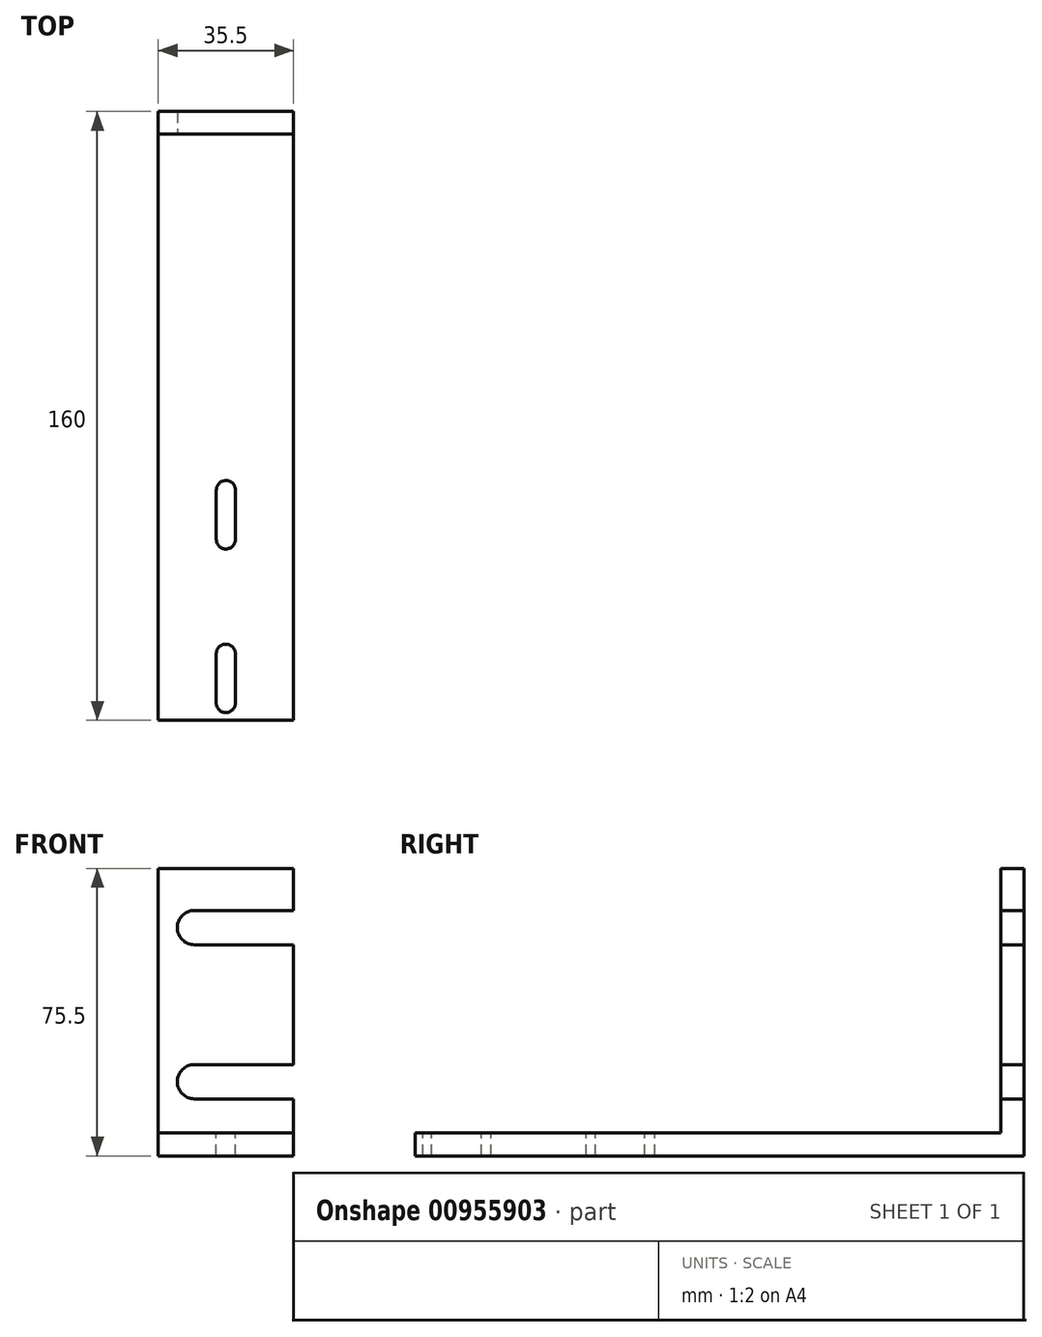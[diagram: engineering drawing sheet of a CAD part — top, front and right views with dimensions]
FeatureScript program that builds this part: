
annotation { "Feature Type Name" : "Feature", "Feature Type Description" : "" }
export const myFeature = defineFeature(function(context is Context, id is Id, definition is map)
    precondition{}
    {
        {
            var Q0;
            Q0=qCreatedBy(makeId("Front.planeOp"),FACE);
            var sketch = newSketch(context, id + "F0", { "sketchPlane" : qUnion([Q0])});
            skLineSegment(sketch, "E0.bottom", {"start": v(17.75, 3) * mm, "end": v(-17.75, 3) * mm});
            skLineSegment(sketch, "E0.top", {"start": v(17.75, -3) * mm, "end": v(-17.75, -3) * mm});
            skLineSegment(sketch, "E0.left", {"start": v(17.75, 3) * mm, "end": v(17.75, -3) * mm});
            skLineSegment(sketch, "E0.right", {"start": v(-17.75, 3) * mm, "end": v(-17.75, -3) * mm});
            skPoint(sketch, "E0.middle", {"position": v(0, 0) * mm});
            skSolve(sketch);
        }
        {
            var Q0;
            Q0=makeQuery(id+"F0.imprint","IMPRINT",FACE,{"disambiguationData":[TD([[makeQuery(id+"F0.imprint","IMPRINT",EDGE,{"derivedFrom":sQuery(id+"F0.wireOp",EDGE,"E0.bottom")}),1.0]])]});
            extrude(context, id + "F1", {"entities" : qUnion([Q0]), "depth" : 160 * mm, "offsetDistance" : 25 * mm});
        }
        {
            var Q0;
            Q0=makeQuery(id+"F1.opExtrude","SWEPT_FACE",FACE,{"disambiguationData":[OSD([sQuery(id+"F0.wireOp",EDGE,"E0.bottom")])]});
            var sketch = newSketch(context, id + "F2", { "sketchPlane" : qUnion([Q0])});
            skLineSegment(sketch, "E1.bottom", {"start": v(17.75, -6) * mm, "end": v(-17.75, -6) * mm});
            skLineSegment(sketch, "E1.top", {"start": v(17.75, 0) * mm, "end": v(-17.75, 0) * mm});
            skLineSegment(sketch, "E1.left", {"start": v(17.75, -6) * mm, "end": v(17.75, 0) * mm});
            skLineSegment(sketch, "E1.right", {"start": v(-17.75, -6) * mm, "end": v(-17.75, 0) * mm});
            skSolve(sketch);
        }
        {
            var Q0;
            Q0=makeQuery(id+"F2.imprint","IMPRINT",FACE,{"disambiguationData":[TD([[makeQuery(id+"F2.imprint","IMPRINT",EDGE,{"derivedFrom":sQuery(id+"F2.wireOp",EDGE,"E1.bottom")}),-1.0]])]});
            extrude(context, id + "F3", {"entities" : qUnion([Q0]), "operationType" : NewBodyOperationType.ADD, "depth" : 69.5 * mm, "offsetDistance" : 25 * mm});
        }
        {
            var Q0;
            Q0=makeQuery(id+"F1.opExtrude","SWEPT_FACE",FACE,{"disambiguationData":[OSD([sQuery(id+"F0.wireOp",EDGE,"E0.bottom")])]});
            var sketch = newSketch(context, id + "F4", { "sketchPlane" : qUnion([Q0])});
            skArc(sketch, "E2", {"start": v(2.5, -142.63) * mm, "mid": v(0.07, -140) * mm, "end": v(-2.5, -142.5) * mm});
            skArc(sketch, "E3", {"start": v(-2.5, -155.5) * mm, "mid": v(0.07, -158) * mm, "end": v(2.5, -155.37) * mm});
            skLineSegment(sketch, "E4", {"start": v(-2.5, -142.5) * mm, "end": v(-2.5, -155.5) * mm});
            skLineSegment(sketch, "E5", {"start": v(2.5, -142.63) * mm, "end": v(2.5, -155.63) * mm});
            skArc(sketch, "E6", {"start": v(2.5, -99.63) * mm, "mid": v(0.07, -97) * mm, "end": v(-2.5, -99.5) * mm});
            skArc(sketch, "E7", {"start": v(-2.5, -112.5) * mm, "mid": v(0.07, -115) * mm, "end": v(2.5, -112.37) * mm});
            skLineSegment(sketch, "E8", {"start": v(-2.5, -99.5) * mm, "end": v(-2.5, -112.5) * mm});
            skLineSegment(sketch, "E9", {"start": v(2.5, -99.63) * mm, "end": v(2.5, -112.63) * mm});
            skPoint(sketch, "E10", {"position": v(0, -101.51) * mm});
            skSolve(sketch);
        }
        {
            var Q0;
            {var subQ1=sQuery(id+"F4.wireOp",EDGE,"E6");Q0=makeQuery(id+"F4.imprint","IMPRINT",FACE,{"disambiguationData":[TD([[makeQuery(id+"F4.imprint","IMPRINT",EDGE,{"derivedFrom":subQ1}),1.0]])]});}
            extrude(context, id + "F5", {"entities" : qUnion([Q0]), "operationType" : NewBodyOperationType.REMOVE, "oppositeDirection" : true, "depth" : 25 * mm, "offsetDistance" : 25 * mm});
        }
        {
            var Q0;
            {var subQ1=sQuery(id+"F4.wireOp",EDGE,"E2");Q0=makeQuery(id+"F4.imprint","IMPRINT",FACE,{"disambiguationData":[TD([[makeQuery(id+"F4.imprint","IMPRINT",EDGE,{"derivedFrom":subQ1}),1.0]])]});}
            extrude(context, id + "F6", {"entities" : qUnion([Q0]), "operationType" : NewBodyOperationType.REMOVE, "oppositeDirection" : true, "depth" : 25 * mm, "offsetDistance" : 25 * mm});
        }
        {
            var Q0;
            Q0=makeQuery(id+"F3.opExtrude","SWEPT_FACE",FACE,{"disambiguationData":[OSD([sQuery(id+"F2.wireOp",EDGE,"E1.bottom")])]});
            var sketch = newSketch(context, id + "F7", { "sketchPlane" : qUnion([Q0])});
            skArc(sketch, "E11", {"start": v(-8.25, 21) * mm, "mid": v(-12.75, 16.5) * mm, "end": v(-8.25, 12) * mm});
            skLineSegment(sketch, "E12", {"start": v(-8.25, 21) * mm, "end": v(17.75, 21) * mm});
            skLineSegment(sketch, "E13", {"start": v(-8.25, 12) * mm, "end": v(17.75, 12) * mm});
            skArc(sketch, "E14", {"start": v(-8.25, 61.5) * mm, "mid": v(-12.75, 57) * mm, "end": v(-8.25, 52.5) * mm});
            skLineSegment(sketch, "E15", {"start": v(-8.25, 61.5) * mm, "end": v(17.75, 61.5) * mm});
            skLineSegment(sketch, "E16", {"start": v(-8.25, 52.5) * mm, "end": v(17.75, 52.5) * mm});
            skSolve(sketch);
        }
        {
            var Q0;
            Q0=makeQuery(id+"F7.imprint","IMPRINT",FACE,{"disambiguationData":[TD([[makeQuery(id+"F7.imprint","IMPRINT",EDGE,{"derivedFrom":sQuery(id+"F7.wireOp",EDGE,"E14")}),1.0]])]});
            var Q1;
            Q1=makeQuery(id+"F7.imprint","IMPRINT",FACE,{"disambiguationData":[TD([[makeQuery(id+"F7.imprint","IMPRINT",EDGE,{"derivedFrom":sQuery(id+"F7.wireOp",EDGE,"E11")}),1.0]])]});
            extrude(context, id + "F8", {"entities" : qUnion([Q0, Q1]), "operationType" : NewBodyOperationType.REMOVE, "oppositeDirection" : true, "depth" : 25 * mm, "offsetDistance" : 25 * mm});
        }
    });
